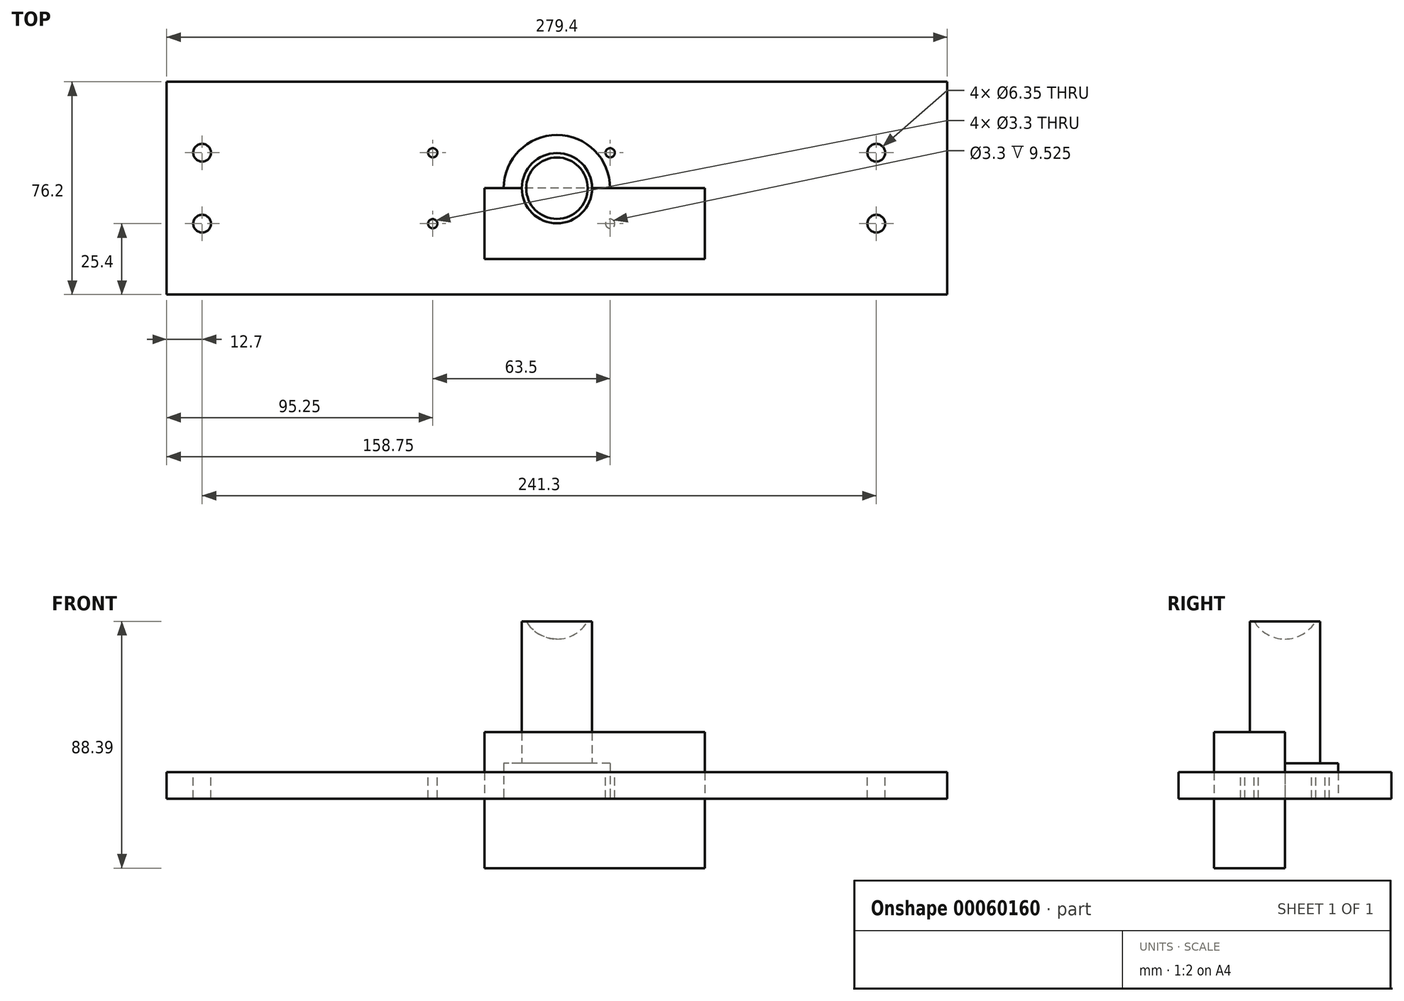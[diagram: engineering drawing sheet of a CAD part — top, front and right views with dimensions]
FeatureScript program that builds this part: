
annotation { "Feature Type Name" : "Feature", "Feature Type Description" : "" }
export const myFeature = defineFeature(function(context is Context, id is Id, definition is map)
    precondition{}
    {
        {
            var Q0;
            Q0=qCreatedBy(makeId("Front.planeOp"),FACE);
            var sketch = newSketch(context, id + "F0", { "sketchPlane" : qUnion([Q0])});
            skLineSegment(sketch, "E0.bottom", {"start": v(-25.98, 23.77) * mm, "end": v(52.94, 23.77) * mm});
            skLineSegment(sketch, "E0.top", {"start": v(-25.98, -24.89) * mm, "end": v(52.94, -24.89) * mm});
            skLineSegment(sketch, "E0.left", {"start": v(-25.98, 23.77) * mm, "end": v(-25.98, -24.89) * mm});
            skLineSegment(sketch, "E0.right", {"start": v(52.94, 23.77) * mm, "end": v(52.94, -24.89) * mm});
            skSolve(sketch);
        }
        {
            var Q0;
            Q0 = qSketchRegion(id + "F0", true);
            extrude(context, id + "F1", {"entities" : qUnion([Q0]), "depth" : 25.4 * mm});
        }
        {
            var Q0;
            Q0=qCreatedBy(makeId("Top.planeOp"),FACE);
            var sketch = newSketch(context, id + "F2", { "sketchPlane" : qUnion([Q0])});
            skLineSegment(sketch, "E1.bottom", {"start": v(-139.7, -38.1) * mm, "end": v(139.7, -38.1) * mm});
            skLineSegment(sketch, "E1.top", {"start": v(-139.7, 38.1) * mm, "end": v(139.7, 38.1) * mm});
            skLineSegment(sketch, "E1.left", {"start": v(-139.7, -38.1) * mm, "end": v(-139.7, 38.1) * mm});
            skLineSegment(sketch, "E1.right", {"start": v(139.7, -38.1) * mm, "end": v(139.7, 38.1) * mm});
            skLineSegment(sketch, "E2", {"start": v(0, 38.1) * mm, "end": v(0, 0) * mm});
            skLineSegment(sketch, "E3", {"start": v(0, 0) * mm, "end": v(139.7, 0) * mm});
            skSolve(sketch);
        }
        {
            var Q0;
            Q0 = qSketchRegion(id + "F2", true);
            extrude(context, id + "F3", {"entities" : qUnion([Q0]), "depth" : 9.52 * mm});
        }
        {
            var Q0;
            Q0=makeQuery(id+"F3.opExtrude","CAP_FACE",FACE,{"disambiguationData":[OSD([sQuery(id+"F2.wireOp",EDGE,"E1.bottom"),sQuery(id+"F2.wireOp",EDGE,"E1.top"),sQuery(id+"F2.wireOp",EDGE,"E1.left"),sQuery(id+"F2.wireOp",EDGE,"E1.right")])],"isStart":false});
            var sketch = newSketch(context, id + "F4", { "sketchPlane" : qUnion([Q0])});
            skCircle(sketch, "E4", {"center": v(114.3, 12.7) * mm, "radius": 3.18 * mm});
            skCircle(sketch, "E5.MirrorC", {"center": v(114.3, -12.7) * mm, "radius": 3.18 * mm});
            skCircle(sketch, "E6", {"center": v(19.05, 12.7) * mm, "radius": 1.65 * mm});
            skCircle(sketch, "E7.MirrorC", {"center": v(19.05, -12.7) * mm, "radius": 1.65 * mm});
            skCircle(sketch, "E8", {"center": v(-127, 12.7) * mm, "radius": 3.18 * mm});
            skCircle(sketch, "E9", {"center": v(-44.45, 12.7) * mm, "radius": 1.65 * mm});
            skCircle(sketch, "E10.MirrorC", {"center": v(-44.45, -12.7) * mm, "radius": 1.65 * mm});
            skCircle(sketch, "E11.MirrorC", {"center": v(-127, -12.7) * mm, "radius": 3.18 * mm});
            skSolve(sketch);
        }
        {
            var Q0;
            Q0 = qSketchRegion(id + "F4", true);
            extrude(context, id + "F5", {"entities" : qUnion([Q0]), "operationType" : NewBodyOperationType.REMOVE, "oppositeDirection" : true, "depth" : 9.52 * mm});
        }
        {
            var Q0;
            Q0=qCreatedBy(makeId("Top.planeOp"),FACE);
            var sketch = newSketch(context, id + "F6", { "sketchPlane" : qUnion([Q0])});
            skCircle(sketch, "E12", {"center": v(0, 0) * mm, "radius": 19.05 * mm});
            skSolve(sketch);
        }
        {
            var Q0;
            Q0 = qSketchRegion(id + "F6", true);
            extrude(context, id + "F7", {"entities" : qUnion([Q0]), "depth" : 12.7 * mm});
        }
        {
            var Q0;
            Q0=makeQuery(id+"F7.opExtrude","CAP_FACE",FACE,{"disambiguationData":[OSD([sQuery(id+"F6.wireOp",EDGE,"E12")])],"isStart":false});
            var sketch = newSketch(context, id + "F8", { "sketchPlane" : qUnion([Q0])});
            skCircle(sketch, "E13", {"center": v(0, 0) * mm, "radius": 12.57 * mm});
            skSolve(sketch);
        }
        {
            var Q0;
            Q0 = qSketchRegion(id + "F8", true);
            extrude(context, id + "F9", {"entities" : qUnion([Q0]), "operationType" : NewBodyOperationType.ADD, "depth" : 50.8 * mm});
        }
        {
            var Q0;
            Q0=qCreatedBy(makeId("Front.planeOp"),FACE);
            var sketch = newSketch(context, id + "F10", { "sketchPlane" : qUnion([Q0])});
            skArc(sketch, "E14", {"start": v(0, 57.15) * mm, "mid": v(8.98, 60.87) * mm, "end": v(12.7, 69.85) * mm});
            skLineSegment(sketch, "E15", {"start": v(0, 69.85) * mm, "end": v(0, 57.15) * mm});
            skLineSegment(sketch, "E16", {"start": v(0, 69.85) * mm, "end": v(12.7, 69.85) * mm});
            skSolve(sketch);
        }
        {
            var Q0;
            Q0 = qSketchRegion(id + "F10", true);
            var Q1;
            Q1=sQuery(id+"F10.wireOp",EDGE,"E15");
            revolve(context, id + "F11", {"operationType" : NewBodyOperationType.REMOVE, "entities" : qUnion([Q0]), "axis" : qUnion([Q1]), "revolveType" : RevolveType.FULL, "oppositeDirection" : true});
        }
        {
            var Q0;
            Q0=qCreatedBy(makeId("Top.planeOp"),FACE);
            var sketch = newSketch(context, id + "F12", { "sketchPlane" : qUnion([Q0])});
            skCircle(sketch, "E17", {"center": v(0, 0) * mm, "radius": 19.05 * mm});
            skSolve(sketch);
        }
        {
            var Q0;
            Q0 = qSketchRegion(id + "F12", true);
            extrude(context, id + "F13", {"entities" : qUnion([Q0]), "depth" : 12.7 * mm});
        }
        {
            var Q0;
            Q0=makeQuery(id+"F13.opExtrude","CAP_FACE",FACE,{"disambiguationData":[OSD([sQuery(id+"F12.wireOp",EDGE,"E17")])],"isStart":false});
            var sketch = newSketch(context, id + "F14", { "sketchPlane" : qUnion([Q0])});
            skCircle(sketch, "E18", {"center": v(0, 0) * mm, "radius": 12.57 * mm});
            skSolve(sketch);
        }
        {
            var Q0;
            Q0 = qSketchRegion(id + "F14", true);
            extrude(context, id + "F15", {"entities" : qUnion([Q0]), "operationType" : NewBodyOperationType.ADD, "depth" : 50.8 * mm});
        }
        {
            var Q0;
            Q0=qCreatedBy(makeId("Front.planeOp"),FACE);
            var sketch = newSketch(context, id + "F16", { "sketchPlane" : qUnion([Q0])});
            skArc(sketch, "E19", {"start": v(0, 57.15) * mm, "mid": v(8.98, 60.87) * mm, "end": v(12.7, 69.85) * mm});
            skLineSegment(sketch, "E20", {"start": v(0, 69.85) * mm, "end": v(0, 57.15) * mm});
            skLineSegment(sketch, "E21", {"start": v(0, 69.85) * mm, "end": v(12.7, 69.85) * mm});
            skPoint(sketch, "E22.orphan", {"position": v(0, 82.55) * mm});
            skSolve(sketch);
        }
        {
            var Q0;
            Q0 = qSketchRegion(id + "F16", true);
            var Q1;
            Q1=sQuery(id+"F16.wireOp",EDGE,"E20");
            revolve(context, id + "F17", {"operationType" : NewBodyOperationType.REMOVE, "entities" : qUnion([Q0]), "axis" : qUnion([Q1]), "revolveType" : RevolveType.FULL});
        }
    });
